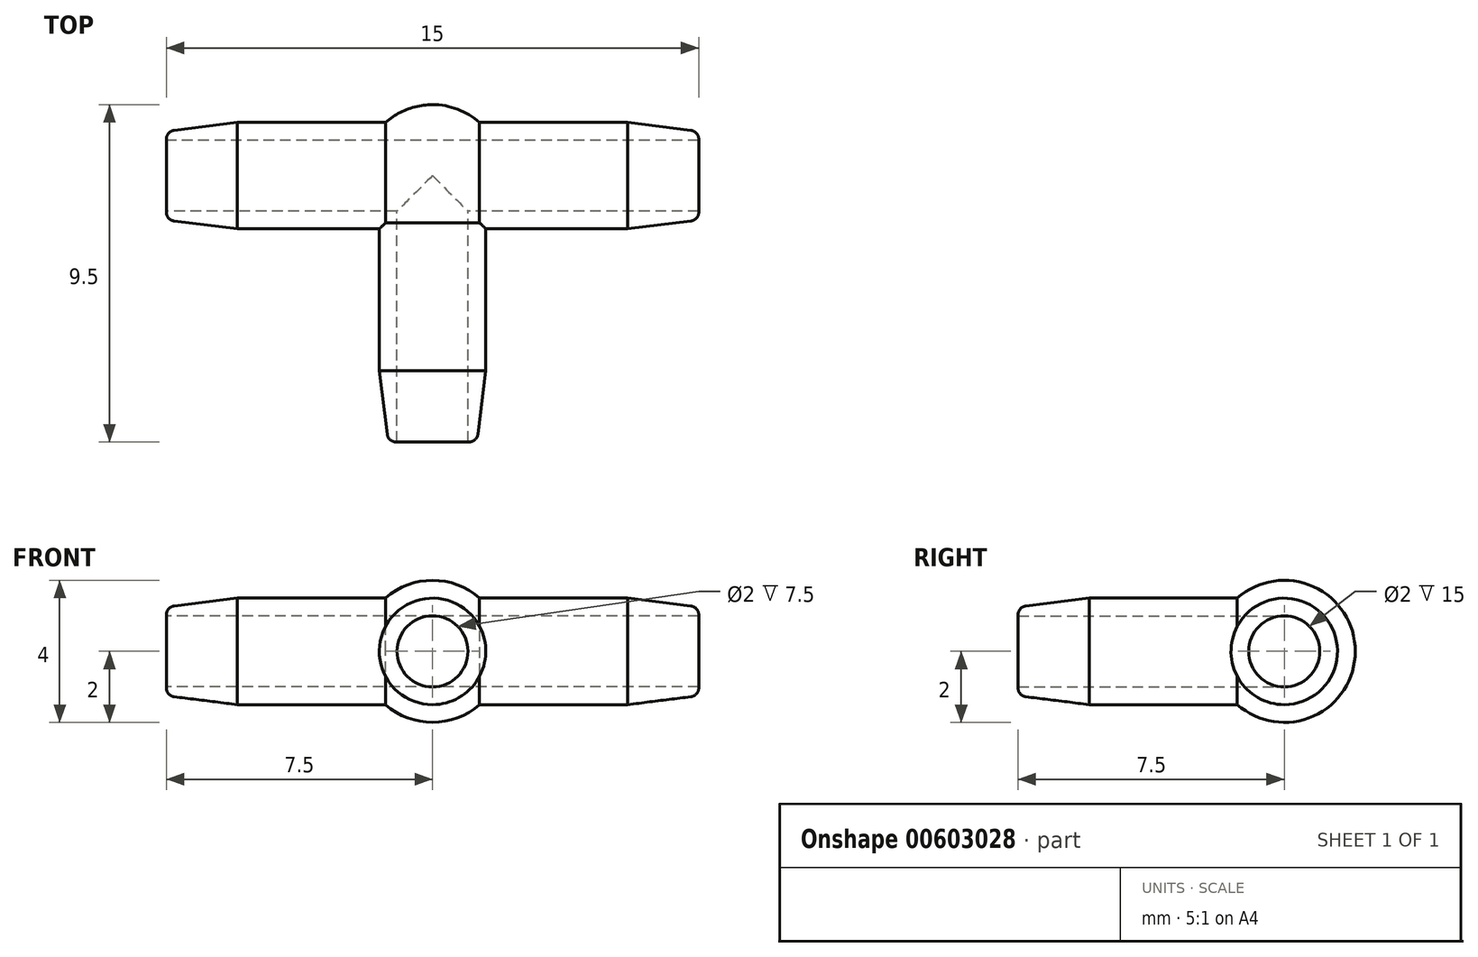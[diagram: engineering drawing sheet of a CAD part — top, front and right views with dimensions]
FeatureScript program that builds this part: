
annotation { "Feature Type Name" : "Feature", "Feature Type Description" : "" }
export const myFeature = defineFeature(function(context is Context, id is Id, definition is map)
    precondition{}
    {
        {
            var Q0;
            Q0=qCreatedBy(makeId("Top.planeOp"),FACE);
            var sketch = newSketch(context, id + "F0", { "sketchPlane" : qUnion([Q0])});
            skArc(sketch, "E0", {"start": v(0, -2) * mm, "mid": v(2, 0) * mm, "end": v(0, 2) * mm});
            skLineSegment(sketch, "E1", {"start": v(0, -2) * mm, "end": v(0, -10.68) * mm, "construction": true});
            skPoint(sketch, "E2.orphan", {"position": v(0, 2) * mm});
            skLineSegment(sketch, "E3", {"start": v(0, -2) * mm, "end": v(0, 2) * mm});
            skSolve(sketch);
        }
        {
            var Q0;
            Q0=makeQuery(id+"F0.imprint","IMPRINT",FACE,{"disambiguationData":[TD([[makeQuery(id+"F0.imprint","IMPRINT",EDGE,{"derivedFrom":sQuery(id+"F0.wireOp",EDGE,"E0")}),1.0]])]});
            var Q1;
            Q1=sQuery(id+"F0.wireOp",EDGE,"E1");
            revolve(context, id + "F1", {"entities" : qUnion([Q0]), "axis" : qUnion([Q1]), "revolveType" : RevolveType.FULL});
        }
        {
            var Q0;
            Q0=qCreatedBy(makeId("Right.planeOp"),FACE);
            var sketch = newSketch(context, id + "F2", { "sketchPlane" : qUnion([Q0])});
            skCircle(sketch, "E4", {"center": v(0, 0) * mm, "radius": 1 * mm});
            skCircle(sketch, "E5.0", {"center": v(0, 0) * mm, "radius": 1.5 * mm});
            skSolve(sketch);
        }
        {
            var Q0;
            Q0 = qSketchRegion(id + "F2", true);
            extrude(context, id + "F3", {"entities" : qUnion([Q0]), "operationType" : NewBodyOperationType.ADD, "endBound" : BoundingType.SYMMETRIC, "depth" : 15 * mm, "offsetDistance" : 25 * mm});
        }
        {
            var Q0;
            Q0=qCreatedBy(makeId("Front.planeOp"),FACE);
            var sketch = newSketch(context, id + "F4", { "sketchPlane" : qUnion([Q0])});
            skCircle(sketch, "E6", {"center": v(0, 0) * mm, "radius": 1 * mm});
            skCircle(sketch, "E7.0", {"center": v(0, 0) * mm, "radius": 1.5 * mm});
            skSolve(sketch);
        }
        {
            var Q0;
            Q0 = qSketchRegion(id + "F4", true);
            extrude(context, id + "F5", {"entities" : qUnion([Q0]), "operationType" : NewBodyOperationType.ADD, "depth" : 7.5 * mm, "offsetDistance" : 25 * mm});
        }
        {
            var Q0;
            Q0=makeQuery(id+"F3.opExtrude","CAP_FACE",FACE,{"disambiguationData":[OSD([sQuery(id+"F2.wireOp",EDGE,"E4"),sQuery(id+"F2.wireOp",EDGE,"E5.0")])],"isStart":false});
            var sketch = newSketch(context, id + "F6", { "sketchPlane" : qUnion([Q0])});
            skCircle(sketch, "E8.0", {"center": v(0, 0) * mm, "radius": 1 * mm});
            skSolve(sketch);
        }
        {
            var Q0;
            Q0 = qSketchRegion(id + "F6", true);
            var Q1;
            Q1=makeQuery(id+"F3.opExtrude","CAP_FACE",FACE,{"disambiguationData":[OSD([sQuery(id+"F2.wireOp",EDGE,"E4"),sQuery(id+"F2.wireOp",EDGE,"E5.0")])],"isStart":true});
            extrude(context, id + "F7", {"entities" : qUnion([Q0]), "operationType" : NewBodyOperationType.REMOVE, "endBound" : BoundingType.UP_TO_SURFACE, "oppositeDirection" : true, "depth" : 25 * mm, "endBoundEntityFace" : qUnion([Q1]), "offsetDistance" : 25 * mm});
        }
        {
            var Q0;
            Q0=makeQuery(id+"F5.opExtrude","CAP_FACE",FACE,{"disambiguationData":[OSD([sQuery(id+"F4.wireOp",EDGE,"E6"),sQuery(id+"F4.wireOp",EDGE,"E7.0")])],"isStart":false});
            var sketch = newSketch(context, id + "F8", { "sketchPlane" : qUnion([Q0])});
            skCircle(sketch, "E9.0", {"center": v(0, 0) * mm, "radius": 1 * mm});
            skSolve(sketch);
        }
        {
            var Q0;
            Q0=makeQuery(id+"F8.imprint","IMPRINT",FACE,{"disambiguationData":[TD([[makeQuery(id+"F8.imprint","IMPRINT",EDGE,{"derivedFrom":sQuery(id+"F8.wireOp",EDGE,"E9.0")}),1.0]])]});
            var Q1;
            {var subQ1=sQuery(id+"F2.wireOp",EDGE,"E5.0");var subQ2=sQuery(id+"F2.wireOp",EDGE,"E4");var subQ3=makeQuery(id+"F3.opExtrude","SWEPT_FACE",FACE,{"disambiguationData":[OSD([subQ2])]});Q1=makeQuery(id+"F7.boolean.opBoolean","MERGE",FACE,{"derivedFrom":[makeQuery(id+"F3.boolean.opBoolean","SPLIT",FACE,{"disambiguationData":[TD([makeQuery(id+"F3.opExtrude","CAP_FACE",FACE,{"disambiguationData":[OSD([subQ2,subQ1])],"isStart":true})])],"derivedFrom":subQ3}),makeQuery(id+"F3.boolean.opBoolean","SPLIT",FACE,{"disambiguationData":[TD([makeQuery(id+"F3.opExtrude","CAP_FACE",FACE,{"disambiguationData":[OSD([subQ2,subQ1])],"isStart":false})])],"derivedFrom":subQ3}),makeQuery(id+"F7.opExtrude","SWEPT_FACE",FACE,{"disambiguationData":[OSD([sQuery(id+"F6.wireOp",EDGE,"E8.0")])]})]});}
            extrude(context, id + "F9", {"entities" : qUnion([Q0]), "operationType" : NewBodyOperationType.REMOVE, "endBound" : BoundingType.UP_TO_SURFACE, "oppositeDirection" : true, "depth" : 25 * mm, "endBoundEntityFace" : qUnion([Q1]), "offsetDistance" : 25 * mm});
        }
        {
            var Q0;
            Q0=makeQuery(id+"F3.opExtrude","CAP_EDGE",EDGE,{"disambiguationData":[OSD([sQuery(id+"F2.wireOp",EDGE,"E5.0")])],"isStart":true});
            chamfer(context, id + "F10", {"entities" : qUnion([Q0]), "chamferType" : ChamferType.TWO_OFFSETS, "width1" : .25 * mm, "oppositeDirection" : true, "width2" : 2 * mm, "tangentPropagation" : true});
        }
        {
            var Q0;
            Q0=makeQuery(id+"F5.opExtrude","CAP_EDGE",EDGE,{"disambiguationData":[OSD([sQuery(id+"F4.wireOp",EDGE,"E7.0")])],"isStart":false});
            chamfer(context, id + "F11", {"entities" : qUnion([Q0]), "chamferType" : ChamferType.TWO_OFFSETS, "width1" : .25 * mm, "oppositeDirection" : false, "width2" : 2 * mm, "tangentPropagation" : true});
        }
        {
            var Q0;
            Q0=makeQuery(id+"F3.opExtrude","CAP_EDGE",EDGE,{"disambiguationData":[OSD([sQuery(id+"F2.wireOp",EDGE,"E5.0")])],"isStart":false});
            chamfer(context, id + "F12", {"entities" : qUnion([Q0]), "chamferType" : ChamferType.TWO_OFFSETS, "width1" : .25 * mm, "oppositeDirection" : false, "width2" : 2 * mm, "tangentPropagation" : true});
        }
        {
            var Q0;
            {var subQ0=sQuery(id+"F2.wireOp",EDGE,"E5.0");Q0=makeQuery(id+"F10.opChamfer","BLEND_EDGE",EDGE,{"blendedFrom":[makeQuery(id+"F3.opExtrude","CAP_EDGE",EDGE,{"disambiguationData":[OSD([subQ0])],"isStart":true}),makeQuery(id+"F3.opExtrude","CAP_FACE",FACE,{"disambiguationData":[OSD([sQuery(id+"F2.wireOp",EDGE,"E4"),subQ0])],"isStart":true})],"blendedInto":[makeQuery(id+"F3.opExtrude","CAP_FACE",FACE,{"disambiguationData":[OSD([sQuery(id+"F2.wireOp",EDGE,"E4"),subQ0])],"isStart":true})]});}
            var Q1;
            {var subQ0=sQuery(id+"F4.wireOp",EDGE,"E7.0");Q1=makeQuery(id+"F11.opChamfer","BLEND_EDGE",EDGE,{"blendedFrom":[makeQuery(id+"F5.opExtrude","CAP_EDGE",EDGE,{"disambiguationData":[OSD([subQ0])],"isStart":false}),makeQuery(id+"F5.opExtrude","CAP_FACE",FACE,{"disambiguationData":[OSD([sQuery(id+"F4.wireOp",EDGE,"E6"),subQ0])],"isStart":false})],"blendedInto":[makeQuery(id+"F5.opExtrude","CAP_FACE",FACE,{"disambiguationData":[OSD([sQuery(id+"F4.wireOp",EDGE,"E6"),subQ0])],"isStart":false})]});}
            var Q2;
            {var subQ0=sQuery(id+"F2.wireOp",EDGE,"E5.0");Q2=makeQuery(id+"F12.opChamfer","BLEND_EDGE",EDGE,{"blendedFrom":[makeQuery(id+"F3.opExtrude","CAP_EDGE",EDGE,{"disambiguationData":[OSD([subQ0])],"isStart":false}),makeQuery(id+"F3.opExtrude","CAP_FACE",FACE,{"disambiguationData":[OSD([sQuery(id+"F2.wireOp",EDGE,"E4"),subQ0])],"isStart":false})],"blendedInto":[makeQuery(id+"F3.opExtrude","CAP_FACE",FACE,{"disambiguationData":[OSD([sQuery(id+"F2.wireOp",EDGE,"E4"),subQ0])],"isStart":false})]});}
            fillet(context, id + "F13", {"entities" : qUnion([Q0, Q1, Q2]), "radius" : .25 * mm, "tangentPropagation" : true, "allowEdgeOverflow" : false});
        }
    });
